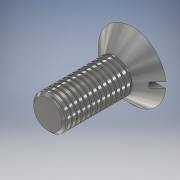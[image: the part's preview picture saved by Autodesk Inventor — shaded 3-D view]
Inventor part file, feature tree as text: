
AUTODESK INVENTOR PART (.ipt)
format: ipt  version: 2018 (Build 220112000, 112)  size: 324,096 bytes
history: native  units: mm
features: sketch x3, revolve x1, extrude x1, chamfer x1, helix x1
ambient origin geometry x8: Origin, YZ Plane, XZ Plane, XY Plane, X Axis, Y Axis, Z Axis, Center Point
bodies: Solid1 (feature_tree)
feature tree (7):
  revolve  "Revolution1"  [1 undecoded]
  extrude  "Extrusion1"  TaperAngle=90.0deg  [1 undecoded]
  chamfer  "Chamfer1"  Distance=1.0mm
  helix  "Coil1"  [1 undecoded]
  sketch  "Sketch1"  dims[d0=30.0mm d1=12.0mm]
  sketch  "Sketch2"  dims[d3=135.0deg d4=90.0deg]
  sketch  "Sketch3"  dims[d5=2.0mm d6=1.0mm d7=3.0mm d8=0.0mm d9=1.0mm d10=2.0mm d11=45.0deg d12=0.31mm d13=0.31mm d14=60.0deg d15=30.0deg d16=1.75mm d17=24.0mm d18=10.0mm d19=0.0mm d20=90.0deg d21=90.0deg d22=0.0mm d23=0.0mm]
note: 3 required parameter values undecoded (feature->parameter linkage not recoverable at this tier; creation-order binding heuristic only, values carry confidence <= 0.55)